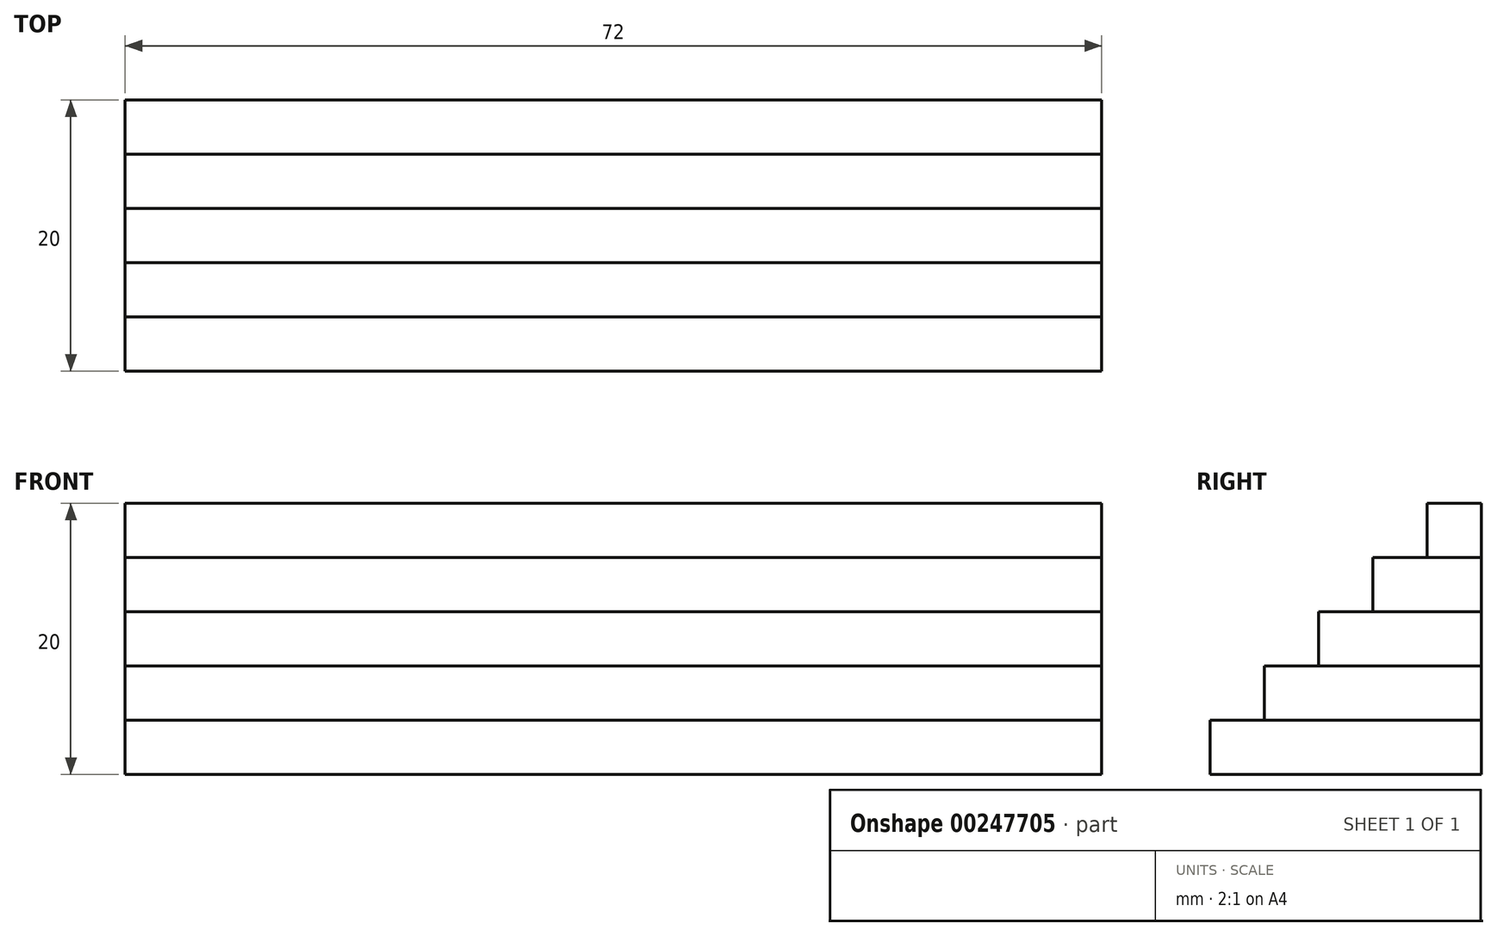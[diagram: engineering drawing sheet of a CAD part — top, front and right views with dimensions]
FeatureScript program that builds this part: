
annotation { "Feature Type Name" : "Feature", "Feature Type Description" : "" }
export const myFeature = defineFeature(function(context is Context, id is Id, definition is map)
    precondition{}
    {
        {
            var Q0;
            Q0=qCreatedBy(makeId("Top.planeOp"),FACE);
            var sketch = newSketch(context, id + "F0", { "sketchPlane" : qUnion([Q0])});
            skLineSegment(sketch, "E0.bottom", {"start": v(36, -10) * mm, "end": v(-36, -10) * mm});
            skLineSegment(sketch, "E0.top", {"start": v(36, 10) * mm, "end": v(-36, 10) * mm});
            skLineSegment(sketch, "E0.left", {"start": v(36, -10) * mm, "end": v(36, 10) * mm});
            skLineSegment(sketch, "E0.right", {"start": v(-36, -10) * mm, "end": v(-36, 10) * mm});
            skPoint(sketch, "E0.middle", {"position": v(0, 0) * mm});
            skSolve(sketch);
        }
        {
            var Q0;
            Q0 = qSketchRegion(id + "F0", true);
            extrude(context, id + "F1", {"entities" : qUnion([Q0]), "depth" : 4 * mm});
        }
        {
            var Q0;
            Q0=makeQuery(id+"F1.opExtrude","CAP_FACE",FACE,{"disambiguationData":[OSD([sQuery(id+"F0.wireOp",EDGE,"E0.bottom"),sQuery(id+"F0.wireOp",EDGE,"E0.top"),sQuery(id+"F0.wireOp",EDGE,"E0.left"),sQuery(id+"F0.wireOp",EDGE,"E0.right")])],"isStart":false});
            var sketch = newSketch(context, id + "F2", { "sketchPlane" : qUnion([Q0])});
            skLineSegment(sketch, "E1.bottom", {"start": v(-36, 10) * mm, "end": v(36, 10) * mm});
            skLineSegment(sketch, "E1.top", {"start": v(-36, -6) * mm, "end": v(36, -6) * mm});
            skLineSegment(sketch, "E1.left", {"start": v(-36, 10) * mm, "end": v(-36, -6) * mm});
            skLineSegment(sketch, "E1.right", {"start": v(36, 10) * mm, "end": v(36, -6) * mm});
            skSolve(sketch);
        }
        {
            var Q0;
            Q0 = qSketchRegion(id + "F2", true);
            extrude(context, id + "F3", {"entities" : qUnion([Q0]), "depth" : 4 * mm});
        }
        {
            var Q0;
            Q0=makeQuery(id+"F3.opExtrude","CAP_FACE",FACE,{"disambiguationData":[OSD([sQuery(id+"F2.wireOp",EDGE,"E1.bottom"),sQuery(id+"F2.wireOp",EDGE,"E1.top"),sQuery(id+"F2.wireOp",EDGE,"E1.left"),sQuery(id+"F2.wireOp",EDGE,"E1.right")])],"isStart":false});
            var sketch = newSketch(context, id + "F4", { "sketchPlane" : qUnion([Q0])});
            skLineSegment(sketch, "E2.bottom", {"start": v(-36, 10) * mm, "end": v(36, 10) * mm});
            skLineSegment(sketch, "E2.top", {"start": v(-36, -2) * mm, "end": v(36, -2) * mm});
            skLineSegment(sketch, "E2.left", {"start": v(-36, 10) * mm, "end": v(-36, -2) * mm});
            skLineSegment(sketch, "E2.right", {"start": v(36, 10) * mm, "end": v(36, -2) * mm});
            skSolve(sketch);
        }
        {
            var Q0;
            Q0 = qSketchRegion(id + "F4", true);
            extrude(context, id + "F5", {"entities" : qUnion([Q0]), "depth" : 4 * mm});
        }
        {
            var Q0;
            Q0=makeQuery(id+"F5.opExtrude","CAP_FACE",FACE,{"disambiguationData":[OSD([sQuery(id+"F4.wireOp",EDGE,"E2.bottom"),sQuery(id+"F4.wireOp",EDGE,"E2.top"),sQuery(id+"F4.wireOp",EDGE,"E2.left"),sQuery(id+"F4.wireOp",EDGE,"E2.right")])],"isStart":false});
            var sketch = newSketch(context, id + "F6", { "sketchPlane" : qUnion([Q0])});
            skLineSegment(sketch, "E3.bottom", {"start": v(-36, 10) * mm, "end": v(36, 10) * mm});
            skLineSegment(sketch, "E3.top", {"start": v(-36, 2) * mm, "end": v(36, 2) * mm});
            skLineSegment(sketch, "E3.left", {"start": v(-36, 10) * mm, "end": v(-36, 2) * mm});
            skLineSegment(sketch, "E3.right", {"start": v(36, 10) * mm, "end": v(36, 2) * mm});
            skSolve(sketch);
        }
        {
            var Q0;
            Q0 = qSketchRegion(id + "F6", true);
            extrude(context, id + "F7", {"entities" : qUnion([Q0]), "depth" : 4 * mm});
        }
        {
            var Q0;
            Q0=makeQuery(id+"F7.opExtrude","CAP_FACE",FACE,{"disambiguationData":[OSD([sQuery(id+"F6.wireOp",EDGE,"E3.bottom"),sQuery(id+"F6.wireOp",EDGE,"E3.top"),sQuery(id+"F6.wireOp",EDGE,"E3.left"),sQuery(id+"F6.wireOp",EDGE,"E3.right")])],"isStart":false});
            var sketch = newSketch(context, id + "F8", { "sketchPlane" : qUnion([Q0])});
            skLineSegment(sketch, "E4.bottom", {"start": v(-36, 10) * mm, "end": v(36, 10) * mm});
            skLineSegment(sketch, "E4.top", {"start": v(-36, 6) * mm, "end": v(36, 6) * mm});
            skLineSegment(sketch, "E4.left", {"start": v(-36, 10) * mm, "end": v(-36, 6) * mm});
            skLineSegment(sketch, "E4.right", {"start": v(36, 10) * mm, "end": v(36, 6) * mm});
            skSolve(sketch);
        }
        {
            var Q0;
            Q0 = qSketchRegion(id + "F8", true);
            extrude(context, id + "F9", {"entities" : qUnion([Q0]), "depth" : 4 * mm});
        }
    });
